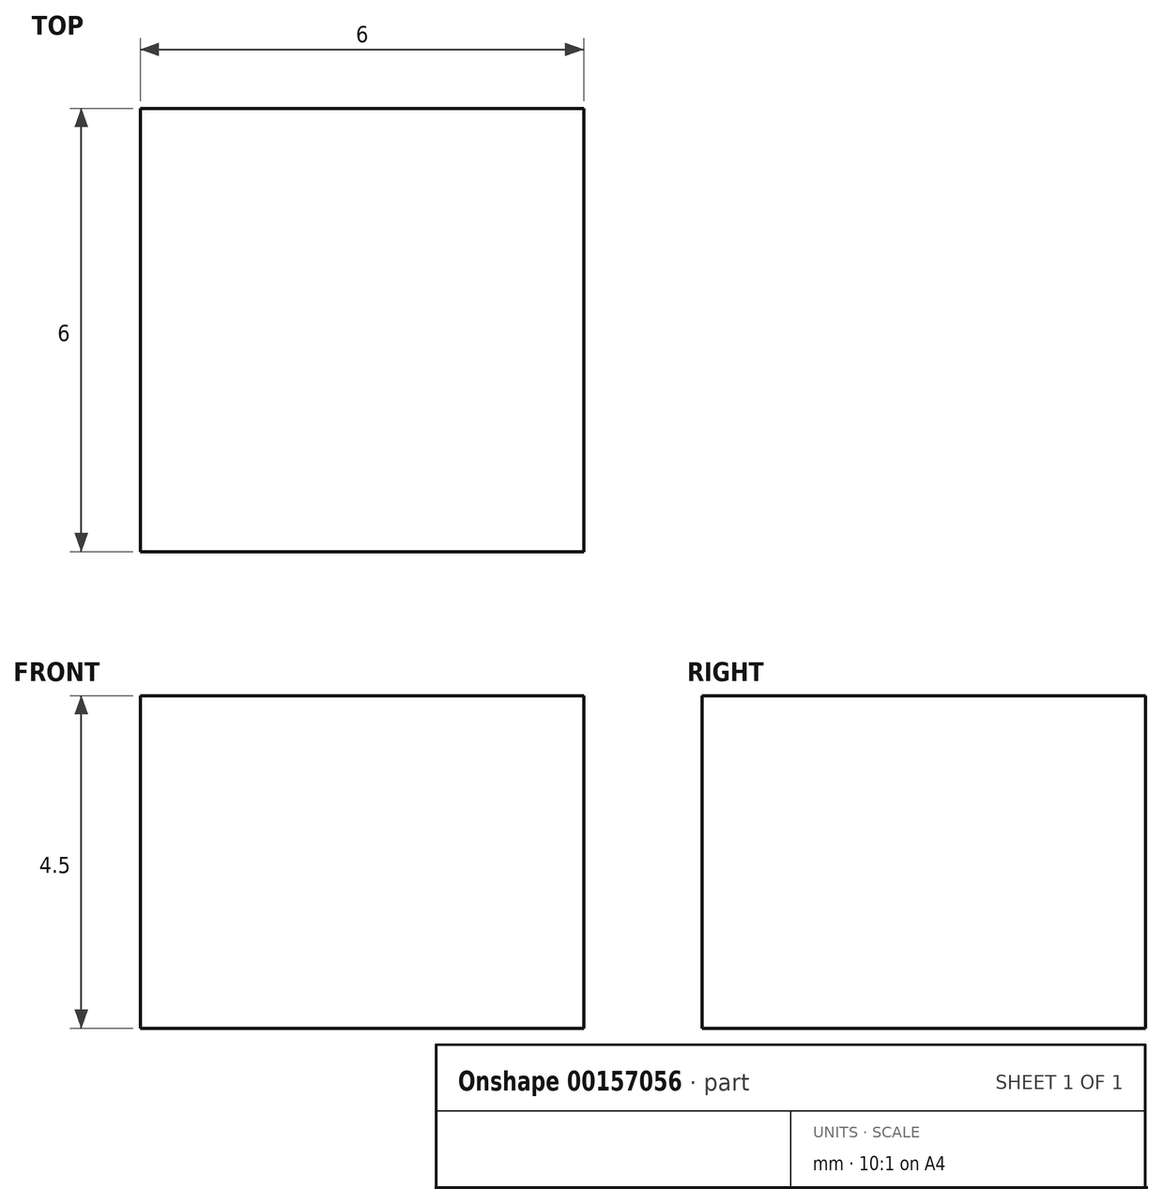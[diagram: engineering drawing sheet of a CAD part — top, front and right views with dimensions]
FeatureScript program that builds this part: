
annotation { "Feature Type Name" : "Feature", "Feature Type Description" : "" }
export const myFeature = defineFeature(function(context is Context, id is Id, definition is map)
    precondition{}
    {
        {
            var Q0;
            Q0=qCreatedBy(makeId("Top.planeOp"),FACE);
            var sketch = newSketch(context, id + "F0", { "sketchPlane" : qUnion([Q0])});
            skLineSegment(sketch, "E0.bottom", {"start": v(-3, 3) * mm, "end": v(3, 3) * mm});
            skLineSegment(sketch, "E0.top", {"start": v(-3, -3) * mm, "end": v(3, -3) * mm});
            skLineSegment(sketch, "E0.left", {"start": v(-3, 3) * mm, "end": v(-3, -3) * mm});
            skLineSegment(sketch, "E0.right", {"start": v(3, 3) * mm, "end": v(3, -3) * mm});
            skPoint(sketch, "E0.middle", {"position": v(0, 0) * mm});
            skSolve(sketch);
        }
        {
            var Q0;
            Q0=makeQuery(id+"F0.imprint","IMPRINT",FACE,{"disambiguationData":[TD([[makeQuery(id+"F0.imprint","IMPRINT",EDGE,{"derivedFrom":sQuery(id+"F0.wireOp",EDGE,"E0.bottom")}),-1.0]])]});
            extrude(context, id + "F1", {"entities" : qUnion([Q0]), "depth" : 4.5 * mm});
        }
    });
